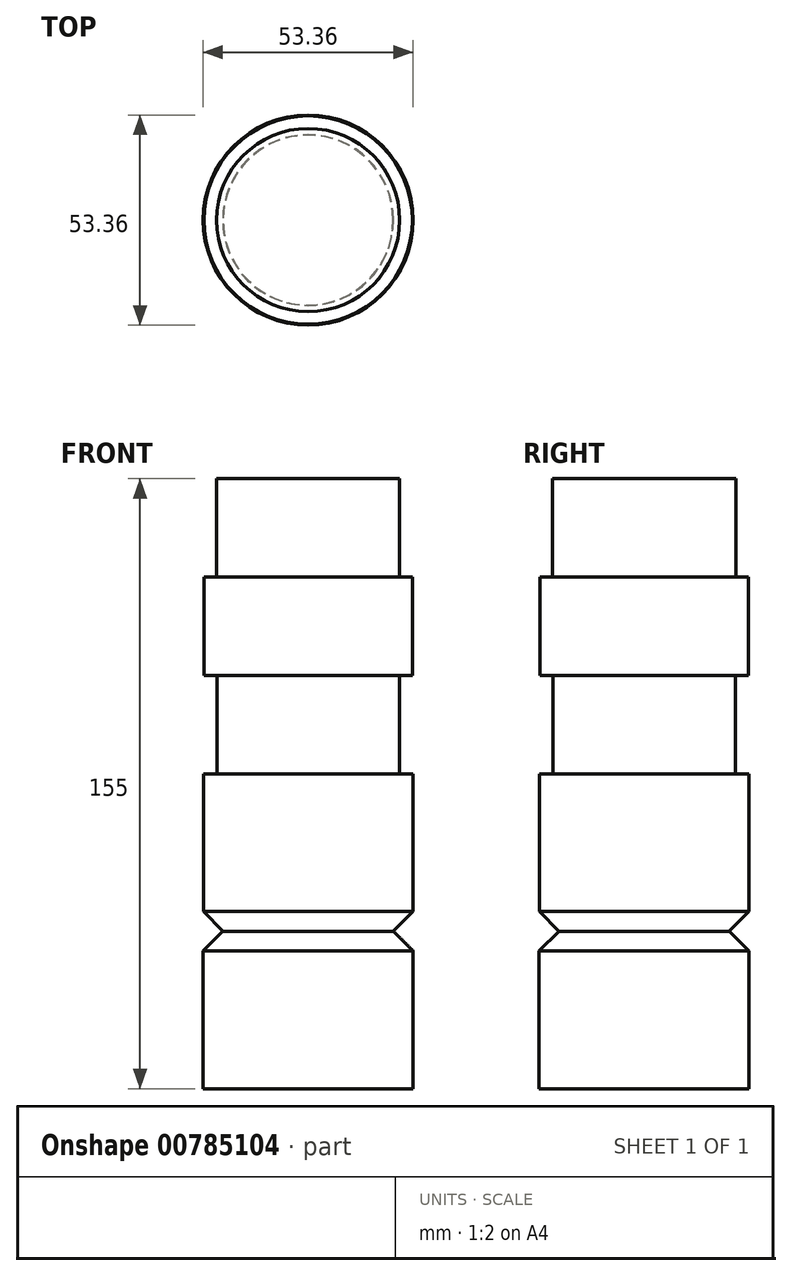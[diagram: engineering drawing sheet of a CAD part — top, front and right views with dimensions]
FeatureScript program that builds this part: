
annotation { "Feature Type Name" : "Feature", "Feature Type Description" : "" }
export const myFeature = defineFeature(function(context is Context, id is Id, definition is map)
    precondition{}
    {
        {
            var Q0;
            Q0=qCreatedBy(makeId("Top.planeOp"),FACE);
            var sketch = newSketch(context, id + "F0", { "sketchPlane" : qUnion([Q0])});
            skCircle(sketch, "E0", {"center": v(0, 0) * mm, "radius": 23.27 * mm});
            skSolve(sketch);
        }
        {
            var Q0;
            Q0 = qSketchRegion(id + "F0", true);
            extrude(context, id + "F1", {"entities" : qUnion([Q0]), "depth" : 25 * mm, "offsetDistance" : 25 * mm});
        }
        {
            var Q0;
            Q0=qCreatedBy(makeId("Top.planeOp"),FACE);
            var sketch = newSketch(context, id + "F2", { "sketchPlane" : qUnion([Q0])});
            skCircle(sketch, "E1", {"center": v(0, 0) * mm, "radius": 26.48 * mm});
            skSolve(sketch);
        }
        {
            var Q0;
            Q0 = qSketchRegion(id + "F2", true);
            extrude(context, id + "F3", {"entities" : qUnion([Q0]), "operationType" : NewBodyOperationType.ADD, "oppositeDirection" : true, "depth" : 25 * mm, "offsetDistance" : 25 * mm});
        }
        {
            var Q0;
            Q0=qCreatedBy(makeId("Top.planeOp"),FACE);
            var sketch = newSketch(context, id + "F4", { "sketchPlane" : qUnion([Q0])});
            skCircle(sketch, "E2", {"center": v(0, 0) * mm, "radius": 23.2 * mm});
            skSolve(sketch);
        }
        {
            var Q0;
            Q0 = qSketchRegion(id + "F4", true);
            extrude(context, id + "F5", {"entities" : qUnion([Q0]), "operationType" : NewBodyOperationType.ADD, "oppositeDirection" : true, "depth" : 50 * mm, "offsetDistance" : 25 * mm});
        }
        {
            var Q0;
            Q0=qCreatedBy(makeId("Top.planeOp"),FACE);
            cPlane(context, id + "F6", {"entities" : qUnion([Q0]), "cplaneType" : CPlaneType.OFFSET, "offset" : 50 * mm, "oppositeDirection" : true, "width" : 150 * mm, "height" : 150 * mm});
        }
        {
            var Q0;
            Q0=qCreatedBy(id+"F6.planeOp",FACE);
            var sketch = newSketch(context, id + "F7", { "sketchPlane" : qUnion([Q0])});
            skCircle(sketch, "E3", {"center": v(0, 0) * mm, "radius": 26.6 * mm});
            skSolve(sketch);
        }
        {
            var Q0;
            Q0 = qSketchRegion(id + "F7", true);
            extrude(context, id + "F8", {"entities" : qUnion([Q0]), "operationType" : NewBodyOperationType.ADD, "oppositeDirection" : true, "depth" : 40 * mm, "offsetDistance" : 25 * mm});
        }
        {
            var Q0;
            Q0=makeQuery(id+"F8.opExtrude","CAP_EDGE",EDGE,{"disambiguationData":[OSD([sQuery(id+"F7.wireOp",EDGE,"E3")])],"isStart":false});
            chamfer(context, id + "F9", {"entities" : qUnion([Q0]), "width" : 5 * mm, "tangentPropagation" : true});
        }
        {
            var Q0;
            Q0=qCreatedBy(id+"F6.planeOp",FACE);
            cPlane(context, id + "F10", {"entities" : qUnion([Q0]), "cplaneType" : CPlaneType.OFFSET, "offset" : 40 * mm, "oppositeDirection" : true, "width" : 150 * mm, "height" : 150 * mm});
        }
        {
            var Q0;
            Q0=qCreatedBy(id+"F10.planeOp",FACE);
            var sketch = newSketch(context, id + "F11", { "sketchPlane" : qUnion([Q0])});
            skCircle(sketch, "E4", {"center": v(0, 0) * mm, "radius": 26.68 * mm});
            skSolve(sketch);
        }
        {
            var Q0;
            Q0 = qSketchRegion(id + "F11", true);
            extrude(context, id + "F12", {"entities" : qUnion([Q0]), "operationType" : NewBodyOperationType.ADD, "oppositeDirection" : true, "depth" : 40 * mm, "offsetDistance" : 25 * mm});
        }
        {
            var Q0;
            Q0=makeQuery(id+"F12.opExtrude","CAP_EDGE",EDGE,{"disambiguationData":[OSD([sQuery(id+"F11.wireOp",EDGE,"E4")])],"isStart":true});
            chamfer(context, id + "F13", {"entities" : qUnion([Q0]), "width" : 5 * mm, "tangentPropagation" : true});
        }
    });
